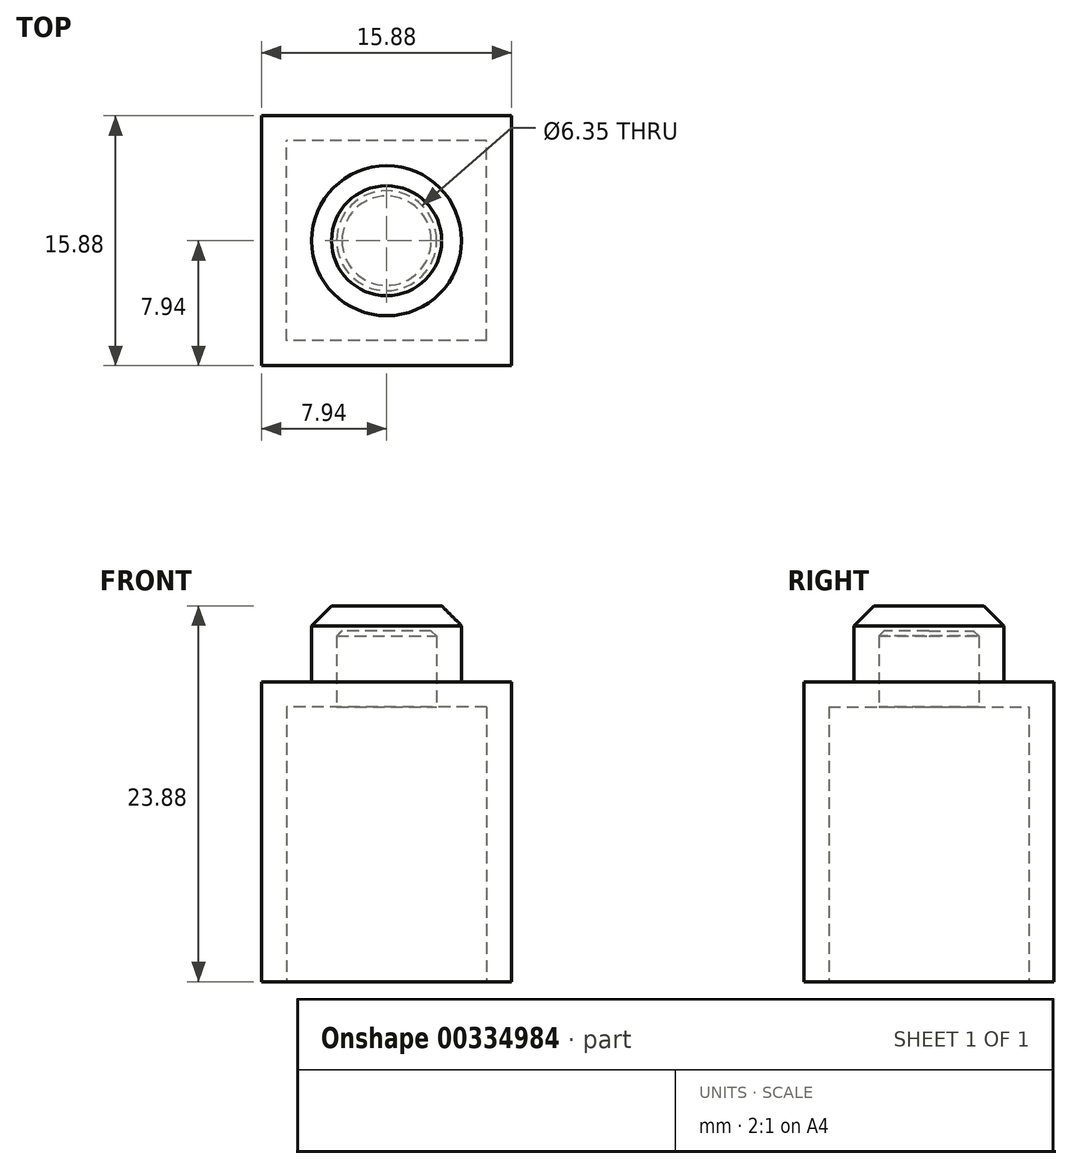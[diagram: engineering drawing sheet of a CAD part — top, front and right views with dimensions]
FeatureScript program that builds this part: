
annotation { "Feature Type Name" : "Feature", "Feature Type Description" : "" }
export const myFeature = defineFeature(function(context is Context, id is Id, definition is map)
    precondition{}
    {
        {
            var Q0;
            Q0=qCreatedBy(makeId("Front.planeOp"),FACE);
            var sketch = newSketch(context, id + "F0", { "sketchPlane" : qUnion([Q0])});
            skLineSegment(sketch, "E0.bottom", {"start": v(7.94, 9.53) * mm, "end": v(-7.94, 9.53) * mm});
            skLineSegment(sketch, "E0.top", {"start": v(7.94, -9.53) * mm, "end": v(-7.94, -9.53) * mm});
            skLineSegment(sketch, "E0.left", {"start": v(7.94, 9.53) * mm, "end": v(7.94, -9.53) * mm});
            skLineSegment(sketch, "E0.right", {"start": v(-7.94, 9.53) * mm, "end": v(-7.94, -9.53) * mm});
            skPoint(sketch, "E0.middle", {"position": v(0, 0) * mm});
            skSolve(sketch);
        }
        {
            var Q0;
            Q0=qSketchRegion(id+"F0",true);
            extrude(context, id + "F1", {"entities" : qUnion([Q0]), "depth" : 15.88 * mm, "symmetric" : true});
        }
        {
            var Q0;
            Q0=makeQuery(id+"F1.opExtrude","SWEPT_FACE",FACE,{"disambiguationData":[OSD([sQuery(id+"F0.wireOp",EDGE,"E0.bottom")])]});
            var sketch = newSketch(context, id + "F2", { "sketchPlane" : qUnion([Q0])});
            skCircle(sketch, "E1", {"center": v(0, 0) * mm, "radius": 4.76 * mm});
            skSolve(sketch);
        }
        {
            var Q0;
            Q0=qSketchRegion(id+"F2",true);
            extrude(context, id + "F3", {"entities" : qUnion([Q0]), "operationType" : NewBodyOperationType.ADD, "depth" : 4.83 * mm});
        }
        {
            var Q0;
            Q0=makeQuery(id+"F3.opExtrude","CAP_EDGE",EDGE,{"disambiguationData":[OSD([sQuery(id+"F2.wireOp",EDGE,"E1")])],"isStart":false});
            var Q1;
            Q1=makeQuery(id+"FdJ1cixTH6ga7Lr_1.0_1.F3.opExtrude","CAP_EDGE",EDGE,{"disambiguationData":[OSD([sQuery(id+"F2.wireOp",EDGE,"E1")])],"isStart":false});
            var Q2;
            Q2=makeQuery(id+"FdJ1cixTH6ga7Lr_1.0_2.F3.opExtrude","CAP_EDGE",EDGE,{"disambiguationData":[OSD([sQuery(id+"F2.wireOp",EDGE,"E1")])],"isStart":false});
            var Q3;
            Q3=makeQuery(id+"FdJ1cixTH6ga7Lr_1.0_3.F3.opExtrude","CAP_EDGE",EDGE,{"disambiguationData":[OSD([sQuery(id+"F2.wireOp",EDGE,"E1")])],"isStart":false});
            var Q4;
            Q4=makeQuery(id+"FdJ1cixTH6ga7Lr_1.1_2.F3.opExtrude","CAP_EDGE",EDGE,{"disambiguationData":[OSD([sQuery(id+"F2.wireOp",EDGE,"E1")])],"isStart":false});
            var Q5;
            Q5=makeQuery(id+"FdJ1cixTH6ga7Lr_1.1_3.F3.opExtrude","CAP_EDGE",EDGE,{"disambiguationData":[OSD([sQuery(id+"F2.wireOp",EDGE,"E1")])],"isStart":false});
            var Q6;
            Q6=makeQuery(id+"FdJ1cixTH6ga7Lr_1.1_1.F3.opExtrude","CAP_EDGE",EDGE,{"disambiguationData":[OSD([sQuery(id+"F2.wireOp",EDGE,"E1")])],"isStart":false});
            var Q7;
            Q7=makeQuery(id+"FdJ1cixTH6ga7Lr_1.1.F3.opExtrude","CAP_EDGE",EDGE,{"disambiguationData":[OSD([sQuery(id+"F2.wireOp",EDGE,"E1")])],"isStart":false});
            chamfer(context, id + "F4", {"entities" : qUnion([Q0, Q1, Q2, Q3, Q4, Q5, Q6, Q7]), "width" : 1.27 * mm, "tangentPropagation" : true});
        }
        {
            var Q0;
            Q0=makeQuery(id+"F1.opExtrude","SWEPT_FACE",FACE,{"disambiguationData":[OSD([sQuery(id+"F0.wireOp",EDGE,"E0.top")])]});
            shell(context, id + "F5", {"entities" : qUnion([Q0]), "thickness" : 1.59 * mm});
        }
    });
